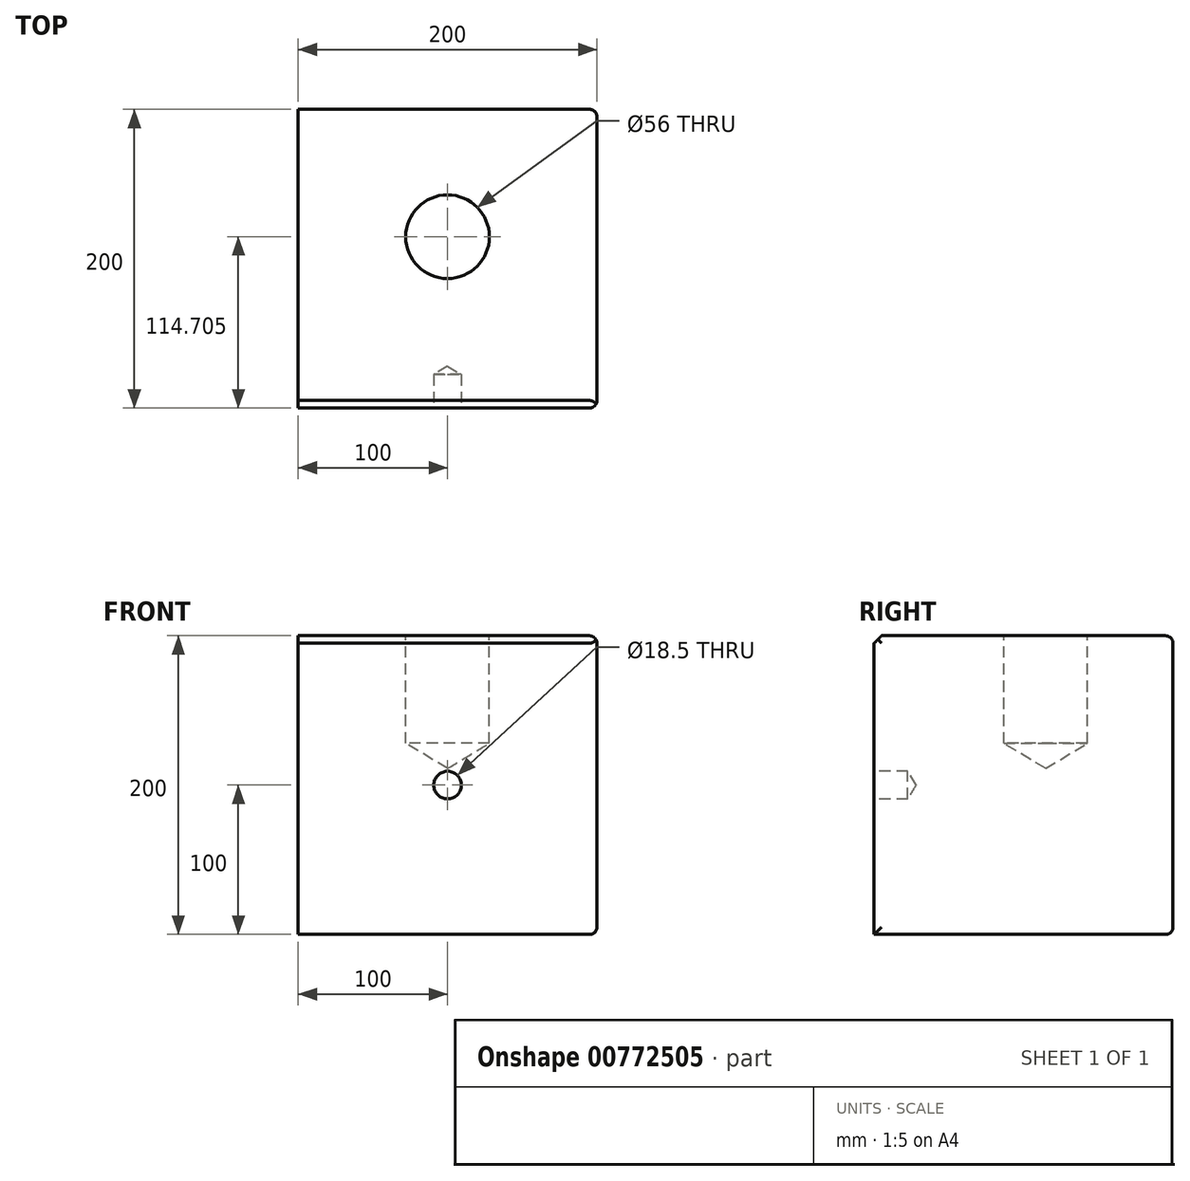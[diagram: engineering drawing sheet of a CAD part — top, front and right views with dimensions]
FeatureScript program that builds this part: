
annotation { "Feature Type Name" : "Feature", "Feature Type Description" : "" }
export const myFeature = defineFeature(function(context is Context, id is Id, definition is map)
    precondition{}
    {
        {
            assignVariable(context, id + "F0", {"name" : "l1", "anyValue" : 200});
        }
        {
            var Q0;
            Q0=qCreatedBy(makeId("Front.planeOp"),FACE);
            var sketch = newSketch(context, id + "F1", { "sketchPlane" : qUnion([Q0])});
            skLineSegment(sketch, "E0.bottom", {"start": v(-100, 100) * mm, "end": v(100, 100) * mm});
            skLineSegment(sketch, "E0.top", {"start": v(-100, -100) * mm, "end": v(100, -100) * mm});
            skLineSegment(sketch, "E0.left", {"start": v(-100, 100) * mm, "end": v(-100, -100) * mm});
            skLineSegment(sketch, "E0.right", {"start": v(100, 100) * mm, "end": v(100, -100) * mm});
            skPoint(sketch, "E0.middle", {"position": v(0, 0) * mm});
            skSolve(sketch);
        }
        {
            var Q0;
            Q0=makeQuery(id+"F1.imprint","IMPRINT",FACE,{"disambiguationData":[TD([[makeQuery(id+"F1.imprint","IMPRINT",EDGE,{"derivedFrom":sQuery(id+"F1.wireOp",EDGE,"E0.bottom")}),-1.0]])]});
            extrude(context, id + "F2", {"entities" : qUnion([Q0]), "endBound" : BoundingType.SYMMETRIC, "depth" : (getVariable(context, 'l1')) * mm, "offsetDistance" : 25.4 * mm});
        }
        {
            var Q0;
            Q0=makeQuery(id+"F2.opExtrude","CAP_FACE",FACE,{"disambiguationData":[OSD([sQuery(id+"F1.wireOp",EDGE,"E0.bottom"),sQuery(id+"F1.wireOp",EDGE,"E0.top"),sQuery(id+"F1.wireOp",EDGE,"E0.left"),sQuery(id+"F1.wireOp",EDGE,"E0.right")])],"isStart":false});
            var sketch = newSketch(context, id + "F3", { "sketchPlane" : qUnion([Q0])});
            skPoint(sketch, "E1", {"position": v(0, 0) * mm});
            skSolve(sketch);
        }
        {
            var Q0;
            Q0=sQuery(id+"F3.wireOp",VERTEX,"E1");
            var Q1;
            Q1=makeQuery(id+"F2.opExtrude","SWEPT_BODY",BODY,{"disambiguationData":[OSD([sQuery(id+"F1.wireOp",EDGE,"E0.bottom"),sQuery(id+"F1.wireOp",EDGE,"E0.top"),sQuery(id+"F1.wireOp",EDGE,"E0.left"),sQuery(id+"F1.wireOp",EDGE,"E0.right")])]});
            hole(context, id + "F4", {"style" : HoleStyle.SIMPLE, "endStyle" : HoleEndStyle.BLIND, "standardTappedOrClearance" : lookupTablePath({ "standard" : "ISO", "engagement" : "75%", "pitch" : "1.5 mm", "size" : "M20", "type" : "Tapped" }), "standardBlindInLast" : lookupTablePath({ "standard" : "ISO", "engagement" : "75%", "pitch" : "1.5 mm", "size" : "M20", "type" : "Tapped" }), "holeDiameter" : 18.5 * mm, "majorDiameter" : 20 * mm, "showTappedDepth" : true, "holeDepth" : 22.5 * mm, "tappedDepth" : 18 * mm, "tapClearance" : 3, "locations" : qUnion([Q0]), "scope" : qUnion([Q1])});
        }
        {
            var Q0;
            Q0=makeQuery(id+"F2.opExtrude","CAP_EDGE",EDGE,{"disambiguationData":[OSD([sQuery(id+"F1.wireOp",EDGE,"E0.bottom")])],"isStart":false});
            chamfer(context, id + "F5", {"entities" : qUnion([Q0]), "width" : 5 * mm, "tangentPropagation" : true});
        }
        {
            var Q0;
            Q0=makeQuery(id+"F2.opExtrude","SWEPT_EDGE",EDGE,{"disambiguationData":[OSD([sQuery(id+"F1.wireOp",EDGE,"E0.bottom"),sQuery(id+"F1.wireOp",EDGE,"E0.right")])]});
            fillet(context, id + "F6", {"entities" : qUnion([Q0]), "radius" : 5 * mm, "tangentPropagation" : true, "allowEdgeOverflow" : false});
        }
        {
            var Q0;
            Q0=makeQuery(id+"F2.opExtrude","SWEPT_FACE",FACE,{"disambiguationData":[OSD([sQuery(id+"F1.wireOp",EDGE,"E0.right")])]});
            fillet(context, id + "F7", {"entities" : qUnion([Q0]), "radius" : 5 * mm, "tangentPropagation" : true, "allowEdgeOverflow" : false});
        }
        {
            var Q0;
            Q0=makeQuery(id+"F2.opExtrude","CAP_EDGE",EDGE,{"disambiguationData":[OSD([sQuery(id+"F1.wireOp",EDGE,"E0.top")])],"isStart":true});
            fillet(context, id + "F8", {"entities" : qUnion([Q0]), "radius" : 5 * mm, "tangentPropagation" : true, "allowEdgeOverflow" : false});
        }
        {
            var Q0;
            Q0=makeQuery(id+"F2.opExtrude","SWEPT_FACE",FACE,{"disambiguationData":[OSD([sQuery(id+"F1.wireOp",EDGE,"E0.bottom")])]});
            var sketch = newSketch(context, id + "F9", { "sketchPlane" : qUnion([Q0])});
            skPoint(sketch, "E2", {"position": v(0, 14.7) * mm});
            skSolve(sketch);
        }
        {
            var Q0;
            Q0=sQuery(id+"F9.wireOp",VERTEX,"E2");
            var Q1;
            Q1=makeQuery(id+"F2.opExtrude","SWEPT_BODY",BODY,{"disambiguationData":[OSD([sQuery(id+"F1.wireOp",EDGE,"E0.bottom"),sQuery(id+"F1.wireOp",EDGE,"E0.top"),sQuery(id+"F1.wireOp",EDGE,"E0.left"),sQuery(id+"F1.wireOp",EDGE,"E0.right")])]});
            hole(context, id + "F10", {"style" : HoleStyle.SIMPLE, "endStyle" : HoleEndStyle.BLIND, "standardTappedOrClearance" : lookupTablePath({ "standard" : "ISO", "engagement" : "75%", "pitch" : "4 mm", "size" : "M60", "type" : "Tapped" }), "standardBlindInLast" : lookupTablePath({ "standard" : "ISO", "fit" : "Normal", "engagement" : "75%", "pitch" : "4 mm", "size" : "M60", "type" : "Clearance & tapped" }), "holeDiameter" : 56 * mm, "majorDiameter" : 60 * mm, "showTappedDepth" : true, "holeDepth" : 72 * mm, "tappedDepth" : 60 * mm, "tapClearance" : 3, "locations" : qUnion([Q0]), "scope" : qUnion([Q1])});
        }
    });
